SOLIDWORKS PART (.sldprt)
format: sldprt  version: not decoded by parser v0  size: 100,864 bytes
history: native  units: mm
features: thread x6, material x1 (+21 scaffold rows collapsed; 3 parser-record rows omitted)
feature tree (31):
  scaffold x21  (default folders/planes/origin — collapsed)
  material  "Material <not specified>"
  parser-record x3  (decoder bookkeeping rows leaked as tree rows — omitted from the tree; the rows remain in map.json)
  thread  "Hole Thread1-1103_Mirrored"  Diameter=6.096mm  [1 undecoded]
  thread  "Hole Thread2-1103_Mirrored"  Diameter=6.096mm  [1 undecoded]
  thread  "Hole Thread3-1103_Mirrored"  Diameter=6.096mm  [1 undecoded]
  thread  "Hole Thread4-1103_Mirrored"  Diameter=6.096mm  [1 undecoded]
  thread  "Hole Thread5-1103_Mirrored"  Diameter=6.096mm  [1 undecoded]
  thread  "Hole Thread6-1103_Mirrored"  Diameter=6.096mm  [1 undecoded]
decode coverage: 6 of 6 modeling features carry decoded parameters
note: 6 parameter values undecoded
note: suppression state not decoded; provenance and decode notes live in map.json
